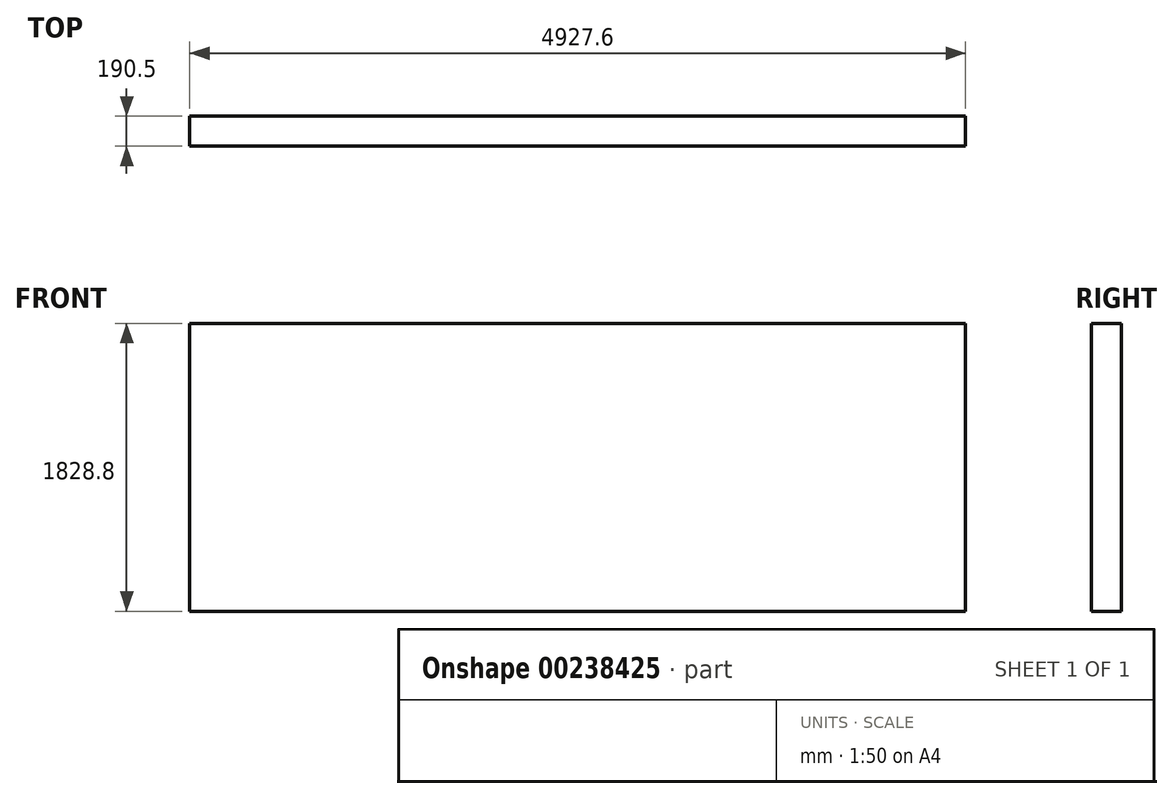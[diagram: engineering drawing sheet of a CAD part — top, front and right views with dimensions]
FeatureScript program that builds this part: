
annotation { "Feature Type Name" : "Feature", "Feature Type Description" : "" }
export const myFeature = defineFeature(function(context is Context, id is Id, definition is map)
    precondition{}
    {
        {
            var Q0;
            Q0=qCreatedBy(makeId("Front.planeOp"),FACE);
            var sketch = newSketch(context, id + "F0", { "sketchPlane" : qUnion([Q0])});
            skLineSegment(sketch, "E0.bottom", {"start": v(-684.21, 960.57) * mm, "end": v(4243.39, 960.57) * mm});
            skLineSegment(sketch, "E0.top", {"start": v(-684.21, -868.23) * mm, "end": v(4243.39, -868.23) * mm});
            skLineSegment(sketch, "E0.left", {"start": v(-684.21, 960.57) * mm, "end": v(-684.21, -868.23) * mm});
            skLineSegment(sketch, "E0.right", {"start": v(4243.39, 960.57) * mm, "end": v(4243.39, -868.23) * mm});
            skSolve(sketch);
        }
        {
            var Q0;
            Q0=makeQuery(id+"F0.imprint","IMPRINT",FACE,{"disambiguationData":[TD([[makeQuery(id+"F0.imprint","IMPRINT",EDGE,{"derivedFrom":sQuery(id+"F0.wireOp",EDGE,"E0.bottom")}),-1.0]])]});
            extrude(context, id + "F1", {"entities" : qUnion([Q0]), "depth" : 190.5 * mm});
        }
    });
